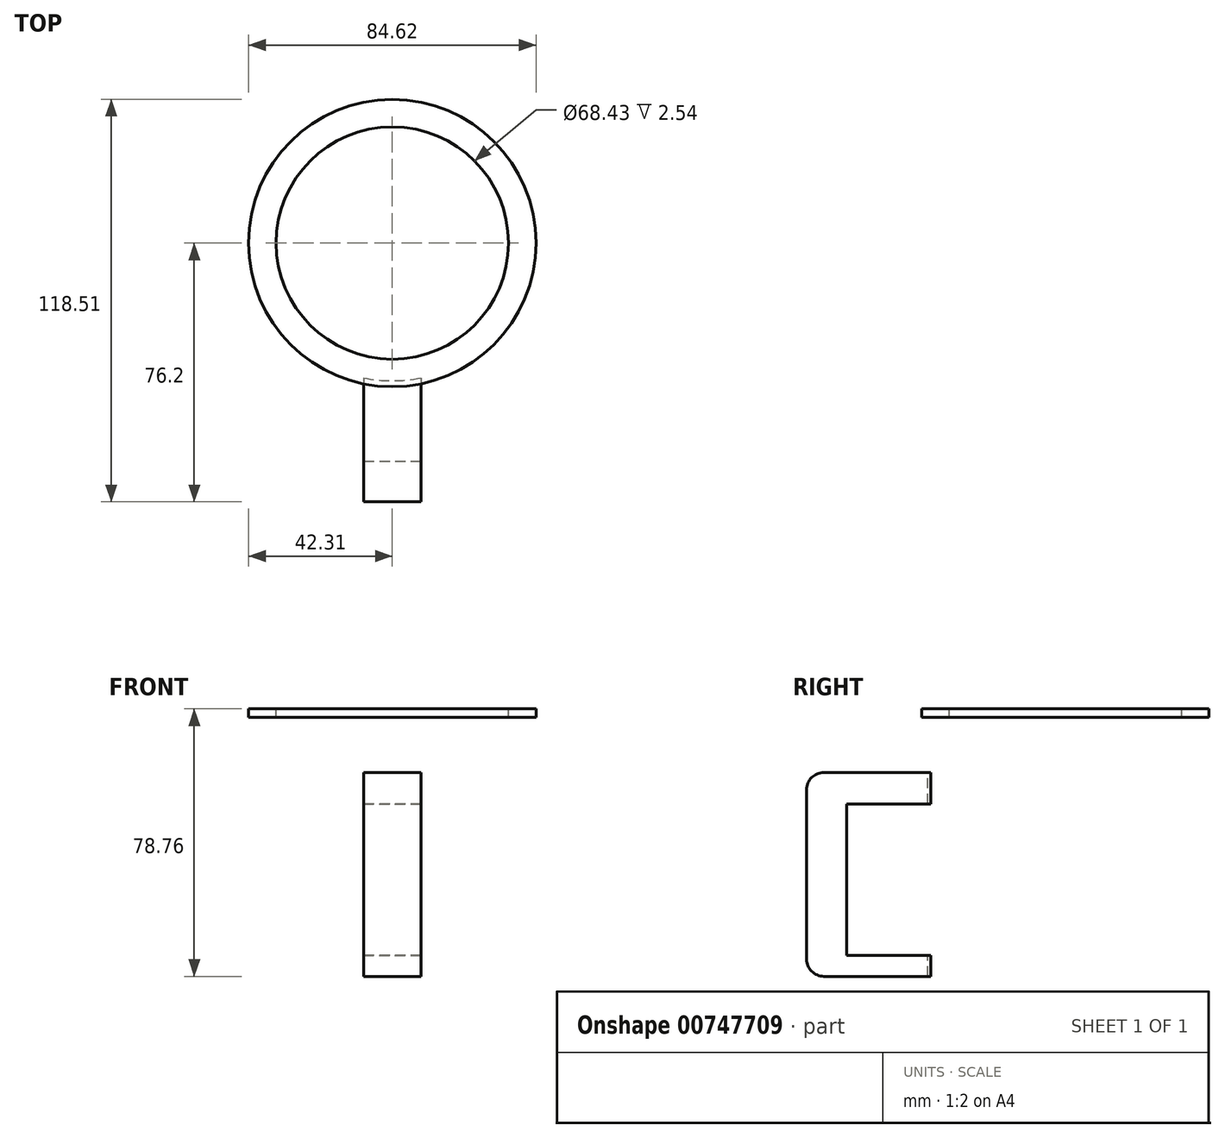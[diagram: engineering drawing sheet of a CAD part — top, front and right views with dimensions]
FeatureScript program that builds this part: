
annotation { "Feature Type Name" : "Feature", "Feature Type Description" : "" }
export const myFeature = defineFeature(function(context is Context, id is Id, definition is map)
    precondition{}
    {
        {
            var Q0;
            Q0=qCreatedBy(makeId("Front.planeOp"),FACE);
            var sketch = newSketch(context, id + "F0", { "sketchPlane" : qUnion([Q0])});
            skLineSegment(sketch, "E0", {"start": v(-40.56, 37.24) * mm, "end": v(-40.56, -39.31) * mm});
            skLineSegment(sketch, "E1", {"start": v(-40.56, -39.31) * mm, "end": v(0, -39.31) * mm});
            skLineSegment(sketch, "E2", {"start": v(-40.56, 37.24) * mm, "end": v(-42.3, 37.24) * mm});
            skLineSegment(sketch, "E3", {"start": v(-42.3, 37.24) * mm, "end": v(-42.3, 43.59) * mm});
            skLineSegment(sketch, "E4.0", {"start": v(-34.21, 43.59) * mm, "end": v(-42.3, 43.59) * mm});
            skLineSegment(sketch, "E5.0", {"start": v(-34.21, -32.96) * mm, "end": v(0, -32.96) * mm});
            skLineSegment(sketch, "E6.0", {"start": v(-34.21, 43.59) * mm, "end": v(-34.21, -32.96) * mm});
            skLineSegment(sketch, "E7", {"start": v(0, -39.31) * mm, "end": v(0, 45.94) * mm});
            skSolve(sketch);
        }
        {
            var Q0;
            Q0=sQuery(id+"F0.wireOp",EDGE,"E6.0");
            var Q1;
            Q1=sQuery(id+"F0.wireOp",EDGE,"E0");
            var Q2;
            Q2=sQuery(id+"F0.wireOp",EDGE,"E4.0");
            var Q3;
            Q3=sQuery(id+"F0.wireOp",EDGE,"E3");
            var Q4;
            Q4=sQuery(id+"F0.wireOp",EDGE,"E2");
            var Q5;
            Q5=sQuery(id+"F0.wireOp",EDGE,"E1");
            var Q6;
            Q6=sQuery(id+"F0.wireOp",EDGE,"E5.0");
            var Q7;
            Q7=sQuery(id+"F0.wireOp",EDGE,"E7");
            revolve(context, id + "F1", {"bodyType" : ToolBodyType.SURFACE, "surfaceOperationType" : NewSurfaceOperationType.NEW, "surfaceEntities" : qUnion([Q0, Q1, Q2, Q3, Q4, Q5, Q6]), "axis" : qUnion([Q7]), "revolveType" : RevolveType.FULL});
        }
        {
            var Q0;
            Q0=makeQuery(id+"F1.opRevolve","SWEPT_FACE",FACE,{"disambiguationData":[OSD([sQuery(id+"F0.wireOp",EDGE,"E4.0")])]});
            extrude(context, id + "F2", {"entities" : qUnion([Q0]), "depth" : 2.54 * mm, "offsetDistance" : 25.4 * mm});
        }
        {
            var Q0;
            Q0=qCreatedBy(makeId("Front.planeOp"),FACE);
            cPlane(context, id + "F3", {"entities" : qUnion([Q0]), "cplaneType" : CPlaneType.OFFSET, "offset" : 50.8 * mm, "width" : 152.4 * mm, "height" : 152.4 * mm});
        }
        {
            var Q0;
            Q0=qCreatedBy(id+"F3.planeOp",FACE);
            var sketch = newSketch(context, id + "F4", { "sketchPlane" : qUnion([Q0])});
            skLineSegment(sketch, "E8.bottom", {"start": v(8.45, 24.88) * mm, "end": v(-8.45, 24.88) * mm});
            skLineSegment(sketch, "E8.top", {"start": v(8.45, 15.63) * mm, "end": v(-8.45, 15.63) * mm});
            skLineSegment(sketch, "E8.left", {"start": v(8.45, 24.88) * mm, "end": v(8.45, 15.63) * mm});
            skLineSegment(sketch, "E8.right", {"start": v(-8.45, 24.88) * mm, "end": v(-8.45, 15.63) * mm});
            skPoint(sketch, "E8.middle", {"position": v(0, 20.26) * mm});
            skSolve(sketch);
        }
        {
            var Q0;
            Q0=makeQuery(id+"F4.imprint","IMPRINT",FACE,{"disambiguationData":[TD([[makeQuery(id+"F4.imprint","IMPRINT",EDGE,{"derivedFrom":sQuery(id+"F4.wireOp",EDGE,"E8.bottom")}),1.0]])]});
            extrude(context, id + "F5", {"entities" : qUnion([Q0]), "endBound" : BoundingType.UP_TO_NEXT, "oppositeDirection" : true, "depth" : 25.4 * mm, "offsetDistance" : 25.4 * mm});
        }
        {
            var Q0;
            Q0=makeQuery(id+"F5.opExtrude","CAP_FACE",FACE,{"disambiguationData":[OSD([sQuery(id+"F4.wireOp",EDGE,"E8.bottom"),sQuery(id+"F4.wireOp",EDGE,"E8.top"),sQuery(id+"F4.wireOp",EDGE,"E8.left"),sQuery(id+"F4.wireOp",EDGE,"E8.right")])],"isStart":true});
            extrude(context, id + "F6", {"entities" : qUnion([Q0]), "operationType" : NewBodyOperationType.ADD, "depth" : 25.4 * mm, "offsetDistance" : 25.4 * mm});
        }
        {
            var Q0;
            {var subQ0=sQuery(id+"F4.wireOp",EDGE,"E8.top");Q0=makeQuery(id+"F6.boolean.opBoolean","MERGE",FACE,{"derivedFrom":[makeQuery(id+"F5.opExtrude","SWEPT_FACE",FACE,{"disambiguationData":[OSD([subQ0])]}),makeQuery(id+"F6.opExtrude","SWEPT_FACE",FACE,{"disambiguationData":[OSD([subQ0])]})]});}
            var sketch = newSketch(context, id + "F7", { "sketchPlane" : qUnion([Q0])});
            skLineSegment(sketch, "E9", {"start": v(8.45, 64.4) * mm, "end": v(-8.45, 64.4) * mm});
            skSolve(sketch);
        }
        {
            var Q0;
            {var subQ0=sQuery(id+"F7.wireOp",EDGE,"E9");Q0=makeQuery(id+"F7.imprint","IMPRINT",FACE,{"disambiguationData":[TD([[makeQuery(id+"F7.imprint","IMPRINT",EDGE,{"derivedFrom":subQ0}),-1.0]])]});}
            extrude(context, id + "F8", {"entities" : qUnion([Q0]), "operationType" : NewBodyOperationType.ADD, "depth" : 50.8 * mm, "offsetDistance" : 25.4 * mm});
        }
        {
            var Q0;
            Q0=makeQuery(id+"F8.opExtrude","SWEPT_FACE",FACE,{"disambiguationData":[OSD([sQuery(id+"F7.wireOp",EDGE,"E9")])]});
            var sketch = newSketch(context, id + "F9", { "sketchPlane" : qUnion([Q0])});
            skLineSegment(sketch, "E10", {"start": v(8.45, -29) * mm, "end": v(-8.45, -29) * mm});
            skSolve(sketch);
        }
        {
            var Q0;
            {var subQ0=sQuery(id+"F9.wireOp",EDGE,"E10");Q0=makeQuery(id+"F9.imprint","IMPRINT",FACE,{"disambiguationData":[TD([[makeQuery(id+"F9.imprint","IMPRINT",EDGE,{"derivedFrom":subQ0}),1.0]])]});}
            extrude(context, id + "F10", {"entities" : qUnion([Q0]), "operationType" : NewBodyOperationType.ADD, "endBound" : BoundingType.UP_TO_NEXT, "depth" : 25.4 * mm, "offsetDistance" : 25.4 * mm});
        }
        {
            var Q0;
            Q0=makeQuery(id+"F6.opExtrude","CAP_EDGE",EDGE,{"disambiguationData":[OSD([sQuery(id+"F4.wireOp",EDGE,"E8.bottom")])],"isStart":false});
            var Q1;
            Q1=makeQuery(id+"F8.opExtrude","CAP_EDGE",EDGE,{"disambiguationData":[OSD([sQuery(id+"F4.wireOp",EDGE,"E8.top")])],"isStart":false});
            fillet(context, id + "F11", {"entities" : qUnion([Q0, Q1]), "radius" : 5.08 * mm, "tangentPropagation" : true, "allowEdgeOverflow" : false});
        }
    });
